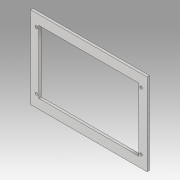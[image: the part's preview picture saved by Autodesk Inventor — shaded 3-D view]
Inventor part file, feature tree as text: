
AUTODESK INVENTOR PART (.ipt)
format: ipt  version: 2019.3 (Build 233278000, 278)  size: 104,960 bytes
history: native  units: mm
features: extrude x1, sketch x1
ambient origin geometry x8: Origin, YZ Plane, XZ Plane, XY Plane, X Axis, Y Axis, Z Axis, Center Point
bodies: Solid1 (feature_tree)
feature tree (2):
  extrude  "Extrusion1"  Depth=77.0mm
  sketch  "Sketch1"  dims[d0=122.0mm d1=77.0mm d2=10.0mm d3=10.0mm d5=11.5mm d6=3.1mm d7=127.6mm d8=63.8mm d9=70.6mm d10=3.2mm d11=3.2mm d12=3.0mm d13=0.0mm d14=100.0mm d15=11.5mm]
